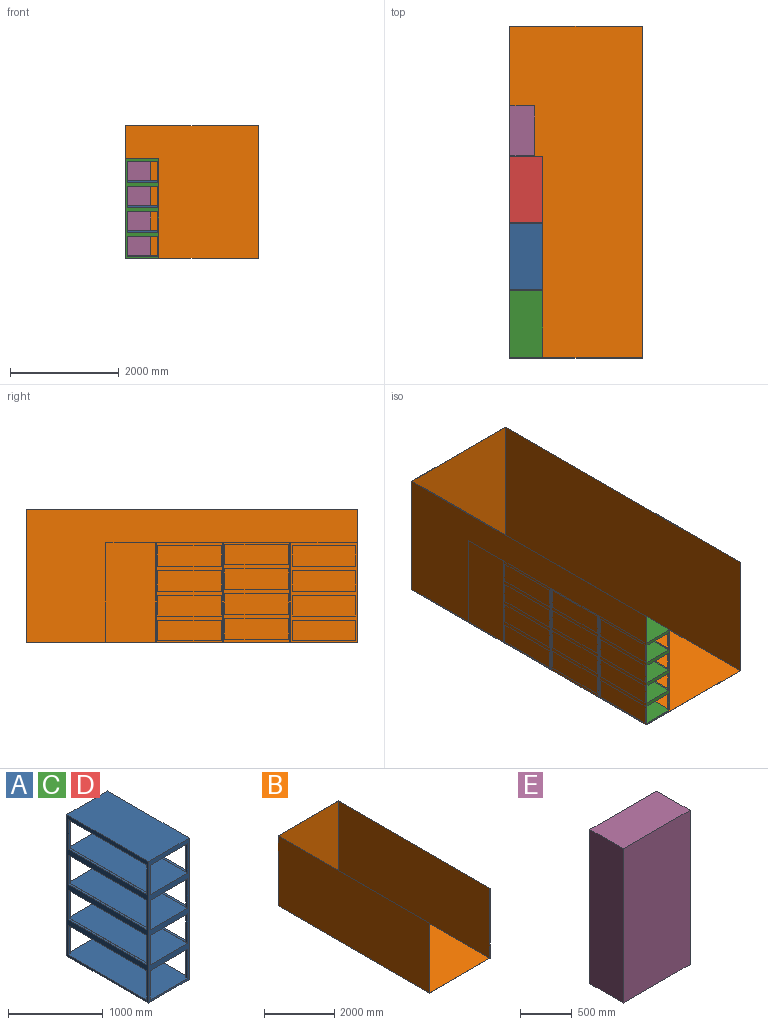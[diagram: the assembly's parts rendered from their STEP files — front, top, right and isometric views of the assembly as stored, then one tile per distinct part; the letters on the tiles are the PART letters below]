
ASSEMBLY  parts=5 mates=8
PART A: 46 faces, bbox 609.6x1219.2x1828.8 mm
  f0: plane 1828.8x609.6mm, normal (0,1,0), area 263225.3mm2, adj f7,f8,f9,f10,f23,f25,f27,f28
  f1: plane 1828.8x609.6mm, normal (0,-1,0), area 263225.3mm2, adj f7,f8,f9,f10,f23,f25,f29,f30
  f2: plane 1168.4x25.4mm, normal (0,0,1), area 29677.4mm2, adj f8,f12,f14,f44
  f3: plane 1168.4x25.4mm, normal (0,0,1), area 29677.4mm2, adj f8,f16,f18,f39
  f4: plane 1168.4x25.4mm, normal (0,0,1), area 29677.4mm2, adj f8,f20,f22,f34
  f5: plane 381x25.4mm, normal (0,1,0), area 9677.4mm2, adj f8,f23,f25,f29
  f6: plane 381x25.4mm, normal (0,-1,0), area 9677.4mm2, adj f8,f23,f25,f28
  f7: plane 1828.8x1219.2mm, normal (1,0,0), area 449031.4mm2, adj f0,f1,f9,f10,f11,f12,f13,f14
  f8: plane 1828.8x1219.2mm, normal (-1,0,0), area 449031.4mm2, adj f0,f1,f2,f3,f4,f5,f6,f9
  f9: plane 1219.2x609.6mm, normal (0,0,1), area 743224.3mm2, adj f0,f1,f7,f8
  f10: plane 1219.2x609.6mm, normal (0,0,-1), area 743224.3mm2, adj f0,f1,f7,f8
  f11: plane 1168.4x25.4mm, normal (0,0,1), area 29677.4mm2, adj f7,f12,f14,f42
  f12: plane 609.6x381mm, normal (0,-1,0), area 21177.1mm2, adj f2,f7,f8,f11,f13,f42,f43,f44
  f13: plane 1168.4x609.6mm, normal (0,0,-1), area 712256.6mm2, adj f7,f8,f12,f14
  f14: plane 609.6x381mm, normal (0,1,0), area 21177.1mm2, adj f2,f7,f8,f11,f13,f42,f44,f45
  f15: plane 1168.4x25.4mm, normal (0,0,1), area 29677.4mm2, adj f7,f16,f18,f37
  f16: plane 609.6x381mm, normal (0,-1,0), area 20569.7mm2, adj f3,f7,f8,f15,f17,f37,f38,f39
  f17: plane 1168.4x609.6mm, normal (0,0,-1), area 712256.6mm2, adj f7,f8,f16,f18
  f18: plane 609.6x381mm, normal (0,1,0), area 20569.7mm2, adj f3,f7,f8,f15,f17,f37,f39,f40
  f19: plane 1168.4x25.4mm, normal (0,0,1), area 29677.4mm2, adj f7,f20,f22,f32
  f20: plane 609.6x381mm, normal (0,-1,0), area 19962.2mm2, adj f4,f7,f8,f19,f21,f32,f33,f34
  f21: plane 1168.4x609.6mm, normal (0,0,-1), area 712256.6mm2, adj f7,f8,f20,f22
  f22: plane 609.6x381mm, normal (0,1,0), area 19962.2mm2, adj f4,f7,f8,f19,f21,f32,f34,f35
  f23: plane 1219.2x609.6mm, normal (0,0,-1), area 740643.7mm2, adj f0,f1,f5,f6,f7,f8,f24,f26
  f24: plane 381x25.4mm, normal (0,1,0), area 9677.4mm2, adj f7,f23,f25,f30
  f25: plane 1219.2x609.6mm, normal (0,0,1), area 740643.7mm2, adj f0,f1,f5,f6,f7,f8,f24,f26
  f26: plane 381x25.4mm, normal (0,-1,0), area 9677.4mm2, adj f7,f23,f25,f27
  f27: plane 381x25.4mm, normal (-1,0,0), area 9677.4mm2, adj f0,f23,f25,f26
  f28: plane 381x25.4mm, normal (1,0,0), area 9677.4mm2, adj f0,f6,f23,f25
  f29: plane 381x25.4mm, normal (1,0,0), area 9677.4mm2, adj f1,f5,f23,f25
  f30: plane 381x25.4mm, normal (-1,0,0), area 9677.4mm2, adj f1,f23,f24,f25
  f31: plane 1219.2x558.8mm, normal (0,0,1), area 681289mm2, adj f0,f1,f32,f34
  f32: plane 1219.2x381mm, normal (-1,0,0), area 20624.9mm2, adj f0,f1,f19,f20,f22,f31,f33,f35
  f33: plane 558.8x25.4mm, normal (0,0,-1), area 14193.5mm2, adj f0,f20,f32,f34
  f34: plane 1219.2x381mm, normal (1,0,0), area 20624.9mm2, adj f0,f1,f4,f20,f22,f31,f33,f35
  f35: plane 558.8x25.4mm, normal (0,0,-1), area 14193.5mm2, adj f1,f22,f32,f34
  f36: plane 1219.2x558.8mm, normal (0,0,1), area 681289mm2, adj f0,f1,f37,f39
  f37: plane 1219.2x381mm, normal (-1,0,0), area 21895mm2, adj f0,f1,f15,f16,f18,f36,f38,f40
  f38: plane 558.8x25.4mm, normal (0,0,-1), area 14193.5mm2, adj f0,f16,f37,f39
  f39: plane 1219.2x381mm, normal (1,0,0), area 21895mm2, adj f0,f1,f3,f16,f18,f36,f38,f40
  f40: plane 558.8x25.4mm, normal (0,0,-1), area 14193.5mm2, adj f1,f18,f37,f39
  f41: plane 1219.2x558.8mm, normal (0,0,1), area 681289mm2, adj f0,f1,f42,f44
  f42: plane 1219.2x381mm, normal (-1,0,0), area 23165mm2, adj f0,f1,f11,f12,f14,f41,f43,f45
  f43: plane 558.8x25.4mm, normal (0,0,-1), area 14193.5mm2, adj f0,f12,f42,f44
  f44: plane 1219.2x381mm, normal (1,0,0), area 23165mm2, adj f0,f1,f2,f12,f14,f41,f43,f45
  f45: plane 558.8x25.4mm, normal (0,0,-1), area 14193.5mm2, adj f1,f14,f42,f44
PART B: 10 faces, bbox 2438.4x6096x2438.4 mm
  f0: plane 2438.4x2438.4mm, normal (0,1,0), area 5945794.6mm2, adj f1,f3,f4,f5
  f1: plane 6096x2438.4mm, normal (-1,0,0), area 14864486.4mm2, adj f0,f2,f4,f5
  f2: plane 2438.4x2438.4mm, normal (0,-1,0), area 18567.7mm2, adj f1,f3,f4,f5,f7,f8,f9
  f3: plane 6096x2438.4mm, normal (1,0,0), area 14864486.4mm2, adj f0,f2,f4,f5
  f4: plane 6096x2438.4mm, normal (0,0,1), area 37148.3mm2, adj f0,f1,f2,f3,f6,f7,f8
  f5: plane 6096x2438.4mm, normal (0,0,-1), area 14864486.4mm2, adj f0,f1,f2,f3
  f6: plane 2435.86x2433.32mm, normal (0,-1,0), area 5927226.9mm2, adj f4,f7,f8,f9
  f7: plane 6093.46x2435.86mm, normal (1,0,0), area 14842815.5mm2, adj f2,f4,f6,f9
  f8: plane 6093.46x2435.86mm, normal (-1,0,0), area 14842815.5mm2, adj f2,f4,f6,f9
  f9: plane 6093.46x2433.32mm, normal (0,0,1), area 14827338.1mm2, adj f2,f6,f7,f8
PART C: same geometry as A
PART D: same geometry as A
PART E: 6 faces, bbox 914.4x457.2x1828.8 mm
  f0: plane 914.4x457.2mm, normal (0,0,1), area 418063.7mm2, adj f1,f3,f4,f5
  f1: plane 1828.8x457.2mm, normal (-1,0,0), area 836127.4mm2, adj f0,f2,f4,f5
  f2: plane 914.4x457.2mm, normal (0,0,-1), area 418063.7mm2, adj f1,f3,f4,f5
  f3: plane 1828.8x457.2mm, normal (1,0,0), area 836127.4mm2, adj f0,f2,f4,f5
  f4: plane 1828.8x914.4mm, normal (0,-1,0), area 1672254.7mm2, adj f0,f1,f2,f3
  f5: plane 1828.8x914.4mm, normal (0,1,0), area 1672254.7mm2, adj f0,f1,f2,f3
PLACE A rot(axis=(1,0,0),180deg) t=(-911.86,-1187.25,1831.34)mm
PLACE B at identity fixed
PLACE C t=(-911.86,-2426.09,2.54)mm
PLACE D t=(-911.86,46.67,2.54)mm
PLACE E rot(axis=(0,0,1),90deg) t=(-1216.66,1125,916.94)mm
MATE planar C.f8 <-> B.f7  axis (-1,0,0) through (-1216.66,-2426.09,975.94)mm
MATE planar E.f2 <-> B.f9  axis (0,0,-1) through (-988.06,1125,2.54)mm
MATE planar B.f9 <-> D.f10  axis (0,0,1) through (0,-1.27,2.54)mm
MATE planar B.f9 <-> A.f9  axis (0,0,1) through (0,-1.27,2.54)mm
MATE planar A.f8 <-> B.f7  axis (-1,0,0) through (-1216.66,-1187.25,857.94)mm
MATE planar E.f5 <-> B.f7  axis (-1,0,0) through (-1216.66,1125,916.94)mm
MATE planar C.f10 <-> B.f9  axis (0,0,-1) through (-911.86,-2426.09,2.54)mm
MATE planar B.f7 <-> D.f8  axis (1,0,0) through (-1216.66,-1.27,1220.47)mm
